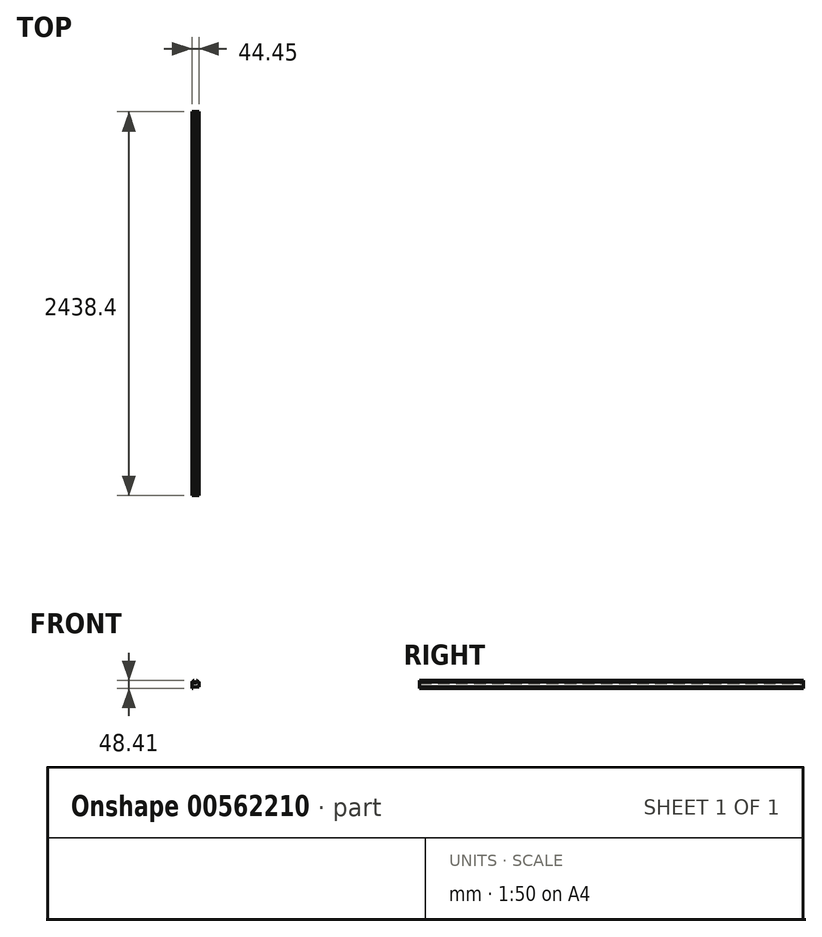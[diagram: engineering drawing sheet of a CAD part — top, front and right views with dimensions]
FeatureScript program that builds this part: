
annotation { "Feature Type Name" : "Feature", "Feature Type Description" : "" }
export const myFeature = defineFeature(function(context is Context, id is Id, definition is map)
    precondition{}
    {
        {
            var Q0;
            Q0=qCreatedBy(makeId("Front.planeOp"),FACE);
            var sketch = newSketch(context, id + "F0", { "sketchPlane" : qUnion([Q0])});
            skLineSegment(sketch, "E0.bottom", {"start": v(-39.62, 0) * mm, "end": v(-43.08, 0) * mm});
            skLineSegment(sketch, "E0.top", {"start": v(-11.54, 48.41) * mm, "end": v(-13.97, 48.41) * mm});
            skLineSegment(sketch, "E0.left", {"start": v(0, 7.48) * mm, "end": v(0, 41.21) * mm});
            skLineSegment(sketch, "E0.right", {"start": v(-44.45, 1.5) * mm, "end": v(-44.45, 41.21) * mm});
            skLineSegment(sketch, "E1", {"start": v(0, 41.21) * mm, "end": v(-2.62, 41.21) * mm});
            skLineSegment(sketch, "E2.0", {"start": v(0, 7.48) * mm, "end": v(-16.26, 7.48) * mm});
            skLineSegment(sketch, "E3.0", {"start": v(-30.48, 34.06) * mm, "end": v(-30.48, 48.41) * mm});
            skLineSegment(sketch, "E4.0", {"start": v(-13.97, 34.06) * mm, "end": v(-13.97, 48.41) * mm});
            skLineSegment(sketch, "E5.0", {"start": v(-35.36, 0.4) * mm, "end": v(-35.36, 7.48) * mm});
            skLineSegment(sketch, "E6.0", {"start": v(-13.97, 34.06) * mm, "end": v(-17.71, 34.06) * mm});
            skLineSegment(sketch, "E7.trimOffspring", {"start": v(-30.48, 48.41) * mm, "end": v(-32.9, 48.41) * mm});
            skLineSegment(sketch, "E8.0", {"start": v(-11.54, 46.1) * mm, "end": v(-11.54, 48.41) * mm});
            skLineSegment(sketch, "E9.0", {"start": v(-35.36, 0.4) * mm, "end": v(-39.62, 0.4) * mm});
            skLineSegment(sketch, "E10.0", {"start": v(-39.62, 0) * mm, "end": v(-39.62, 0.4) * mm});
            skLineSegment(sketch, "E11", {"start": v(-35.36, 7.48) * mm, "end": v(-35.36, 11.83) * mm});
            skLineSegment(sketch, "E12", {"start": v(-35.36, 11.83) * mm, "end": v(-33.19, 11.83) * mm});
            skLineSegment(sketch, "E13", {"start": v(-33.19, 11.83) * mm, "end": v(-33.19, 7.48) * mm});
            skLineSegment(sketch, "E14", {"start": v(-44.45, 1.5) * mm, "end": v(-43.08, 0) * mm});
            skArc(sketch, "E15", {"start": v(-32.9, 46.13) * mm, "mid": v(-37.74, 44.34) * mm, "end": v(-41.83, 41.21) * mm});
            skArc(sketch, "E16", {"start": v(-2.62, 41.21) * mm, "mid": v(-6.71, 44.32) * mm, "end": v(-11.54, 46.1) * mm});
            skLineSegment(sketch, "E17", {"start": v(-16.26, 7.48) * mm, "end": v(-16.26, 9) * mm});
            skLineSegment(sketch, "E18", {"start": v(-16.26, 9) * mm, "end": v(-28.96, 9) * mm});
            skLineSegment(sketch, "E19", {"start": v(-28.96, 9) * mm, "end": v(-28.96, 7.48) * mm});
            skLineSegment(sketch, "E20.trimOffspring", {"start": v(-28.96, 7.48) * mm, "end": v(-33.19, 7.48) * mm});
            skLineSegment(sketch, "E21.trimOffspring", {"start": v(-32.9, 46.13) * mm, "end": v(-32.9, 48.41) * mm});
            skLineSegment(sketch, "E22.trimOffspring", {"start": v(-41.83, 41.21) * mm, "end": v(-44.45, 41.21) * mm});
            skArc(sketch, "E23", {"start": v(-26.74, 34.06) * mm, "mid": v(-22.23, 32.18) * mm, "end": v(-17.71, 34.06) * mm});
            skPoint(sketch, "E23.centerSnap0", {"position": v(-22.23, 34.06) * mm});
            skLineSegment(sketch, "E24.trimOffspring", {"start": v(-26.74, 34.06) * mm, "end": v(-30.48, 34.06) * mm});
            skSolve(sketch);
        }
        {
            var Q0;
            Q0 = qSketchRegion(id + "F0", true);
            extrude(context, id + "F1", {"entities" : qUnion([Q0]), "depth" : 2438.4 * mm, "offsetDistance" : 25.4 * mm});
        }
    });
